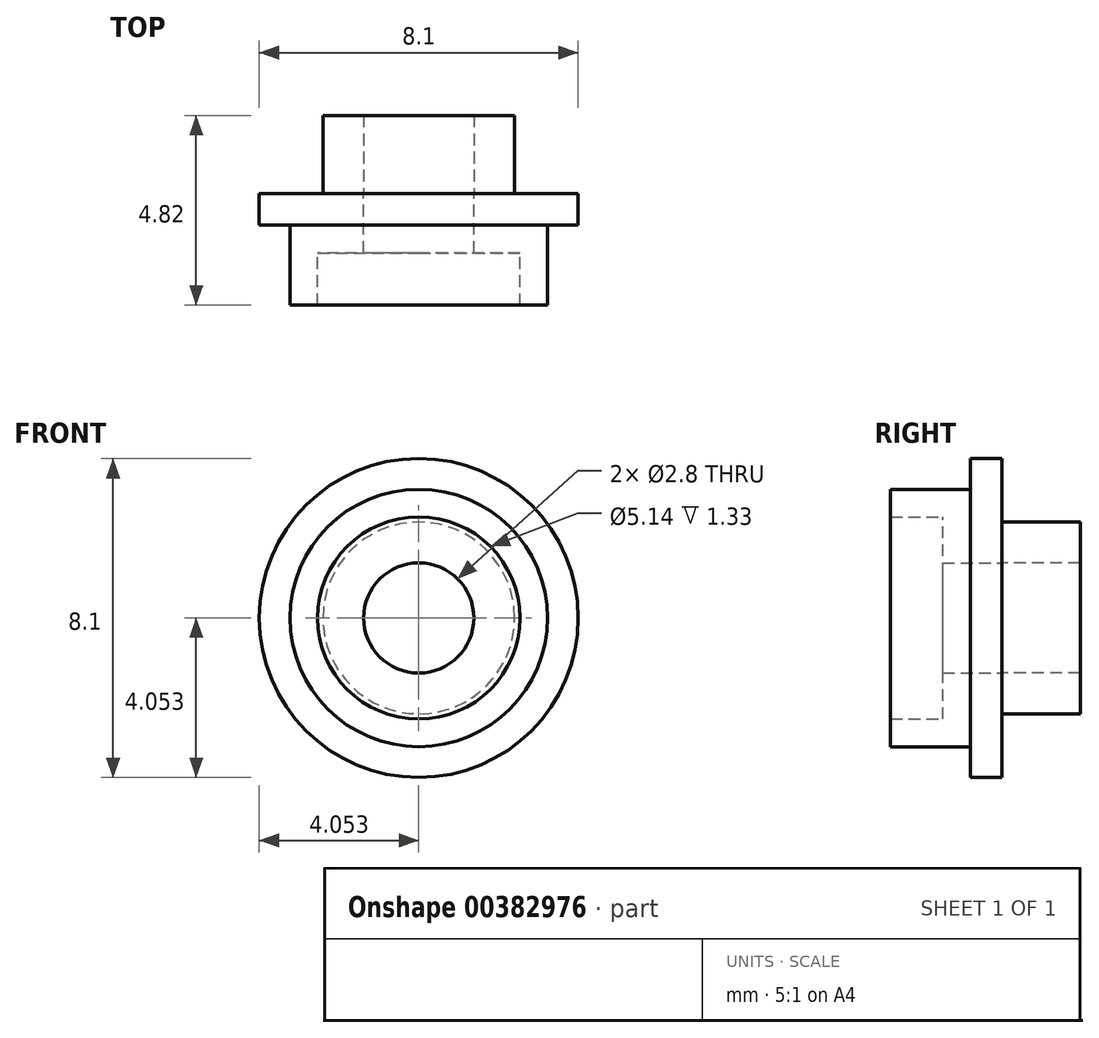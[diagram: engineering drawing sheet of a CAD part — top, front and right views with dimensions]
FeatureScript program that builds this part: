
annotation { "Feature Type Name" : "Feature", "Feature Type Description" : "" }
export const myFeature = defineFeature(function(context is Context, id is Id, definition is map)
    precondition{}
    {
        {
            var Q0;
            Q0=qCreatedBy(makeId("Front.planeOp"),FACE);
            var sketch = newSketch(context, id + "F0", { "sketchPlane" : qUnion([Q0])});
            skCircle(sketch, "E0", {"center": v(12.1, 11.71) * mm, "radius": 3.27 * mm});
            skSolve(sketch);
        }
        {
            var Q0;
            Q0=qSketchRegion(id+"F0",true);
            extrude(context, id + "F1", {"entities" : qUnion([Q0]), "depth" : 2.03 * mm});
        }
        {
            var Q0;
            Q0=makeQuery(id+"F1.opExtrude","CAP_FACE",FACE,{"disambiguationData":[OSD([sQuery(id+"F0.wireOp",EDGE,"E0")])],"isStart":false});
            shell(context, id + "F2", {"entities" : qUnion([Q0]), "thickness" : .70 * mm});
        }
        {
            var Q0;
            Q0=makeQuery(id+"F1.opExtrude","CAP_FACE",FACE,{"disambiguationData":[OSD([sQuery(id+"F0.wireOp",EDGE,"E0")])],"isStart":true});
            var sketch = newSketch(context, id + "F3", { "sketchPlane" : qUnion([Q0])});
            skCircle(sketch, "E1", {"center": v(-12.1, 11.71) * mm, "radius": 4.05 * mm});
            skSolve(sketch);
        }
        {
            var Q0;
            Q0=qSketchRegion(id+"F3",true);
            var Q1;
            {var subQ0=sQuery(id+"F0.wireOp",EDGE,"E0");Q1=makeQuery(id+"F2.opShell","OFFSET_FACE",FACE,{"disambiguationData":[OSD([subQ0]),TDD([makeQuery(id+"F1.opExtrude","CAP_FACE",FACE,{"disambiguationData":[OSD([subQ0])],"isStart":true})])]});}
            extrude(context, id + "F4", {"entities" : qUnion([Q0, Q1]), "operationType" : NewBodyOperationType.ADD, "depth" : .80 * mm});
        }
        {
            var Q0;
            Q0=makeQuery(id+"F4.opExtrude","CAP_FACE",FACE,{"disambiguationData":[OSD([sQuery(id+"F3.wireOp",EDGE,"E1")])],"isStart":false});
            var sketch = newSketch(context, id + "F5", { "sketchPlane" : qUnion([Q0])});
            skCircle(sketch, "E2", {"center": v(-12.1, 11.71) * mm, "radius": 1.4 * mm});
            skSolve(sketch);
        }
        {
            var Q0;
            Q0=makeQuery(id+"F5.imprint","IMPRINT",FACE,{"disambiguationData":[TD([[makeQuery(id+"F5.imprint","IMPRINT",EDGE,{"derivedFrom":sQuery(id+"F5.wireOp",EDGE,"E2")}),1.0]])]});
            extrude(context, id + "F6", {"entities" : qUnion([Q0]), "operationType" : NewBodyOperationType.REMOVE, "oppositeDirection" : true, "depth" : 25 * mm});
        }
        {
            var Q0;
            Q0=makeQuery(id+"F4.opExtrude","CAP_FACE",FACE,{"disambiguationData":[OSD([sQuery(id+"F3.wireOp",EDGE,"E1")])],"isStart":false});
            var sketch = newSketch(context, id + "F7", { "sketchPlane" : qUnion([Q0])});
            skCircle(sketch, "E3", {"center": v(-12.1, 11.71) * mm, "radius": 2.44 * mm});
            skSolve(sketch);
        }
        {
            var Q0;
            Q0=makeQuery(id+"F7.imprint","IMPRINT",FACE,{"disambiguationData":[TD([[makeQuery(id+"F7.imprint","IMPRINT",EDGE,{"derivedFrom":sQuery(id+"F7.wireOp",EDGE,"E3")}),1.0]])]});
            var Q1;
            Q1=makeQuery(id+"F7.imprint","IMPRINT",FACE,{"disambiguationData":[TD([[makeQuery(id+"F7.imprint","IMPRINT",EDGE,{"derivedFrom":makeQuery(id+"F6.boolean.opBoolean","COPY",EDGE,{"derivedFrom":makeQuery(id+"F6.opExtrude","CAP_EDGE",EDGE,{"disambiguationData":[OSD([sQuery(id+"F5.wireOp",EDGE,"E2")])],"isStart":true})})}),1.0]])]});
            var Q2;
            Q2=sQuery(id+"F7.wireOp",EDGE,"E3");
            extrude(context, id + "F8", {"entities" : qUnion([Q0, Q1]), "surfaceEntities" : qUnion([Q2]), "depth" : 1.99 * mm});
        }
    });
